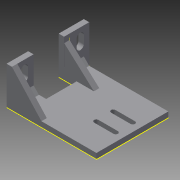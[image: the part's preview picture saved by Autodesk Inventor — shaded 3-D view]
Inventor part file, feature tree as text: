
AUTODESK INVENTOR PART (.ipt)
format: ipt  version: 2014 SP1 (Build 180222100, 222)  size: 186,368 bytes
history: native  units: mm
features: extrude x11, sketch x11, chamfer x2, plane x1
ambient origin geometry x8: Origin, YZ Plane, XZ Plane, XY Plane, X Axis, Y Axis, Z Axis, Center Point
bodies: Solid1 (feature_tree)
feature tree (25):
  extrude  "Extrusion1"  Depth=40.0mm
  extrude  "Extrusion2"  Depth=3.0mm
  extrude  "Extrusion3"  Depth=3.0mm TaperAngle=0.0deg
  extrude  "Extrusion4"  Depth=10.0mm
  extrude  "Extrusion6"  Depth=8.0mm TaperAngle=0.0deg
  extrude  "Extrusion7"  Depth=3.0mm TaperAngle=45.0deg
  sketch  "Sketch8"  dims[d62=-11.0mm d63=3.0mm d64=0.0mm]
  chamfer  "Chamfer1"  Distance=3.0mm Angle=45.0deg
  chamfer  "Chamfer2"  Distance=3.0mm
  sketch  "Sketch11"  dims[d65=3.0mm d66=0.0mm d67=4.0mm]
  plane  "Work Plane1"
  extrude  "Extrusion14"  Depth=4.0mm
  extrude  "Extrusion15"  Depth=3.0mm
  extrude  "Extrusion16"  Depth=2.5mm
  extrude  "Extrusion17"  Depth=2.5mm
  extrude  "Extrusion18"  Depth=10.0mm TaperAngle=0.0deg
  sketch  "Sketch1"  dims[d0=50.0mm d1=40.0mm]
  sketch  "Sketch2"  dims[d2=3.0mm d3=0.0mm d4=3.0mm]
  sketch  "Sketch3"  dims[d5=18.0mm d6=0.0mm d7=3.0mm d8=0.0mm]
  sketch  "Sketch4"  dims[d9=11.0mm d10=10.0mm]
  sketch  "Sketch6"  dims[d11=8.0mm d12=0.0mm d18=1.0mm d19=0.0mm]
  sketch  "Sketch7"  dims[d22=1.0mm d23=0.0mm d37=3.0mm d38=2.0mm d39=45.0deg d40=3.0mm d41=2.0mm d42=45.0deg]
  sketch  "Sketch14"  dims[d68=3.0mm d69=0.0mm d71=4.75mm]
  sketch  "Sketch15"  dims[d72=9.5mm d73=2.5mm]
  sketch  "Sketch16"  dims[d74=10.0mm d75=0.0mm d76=2.5mm d77=10.0mm d78=0.0mm]
